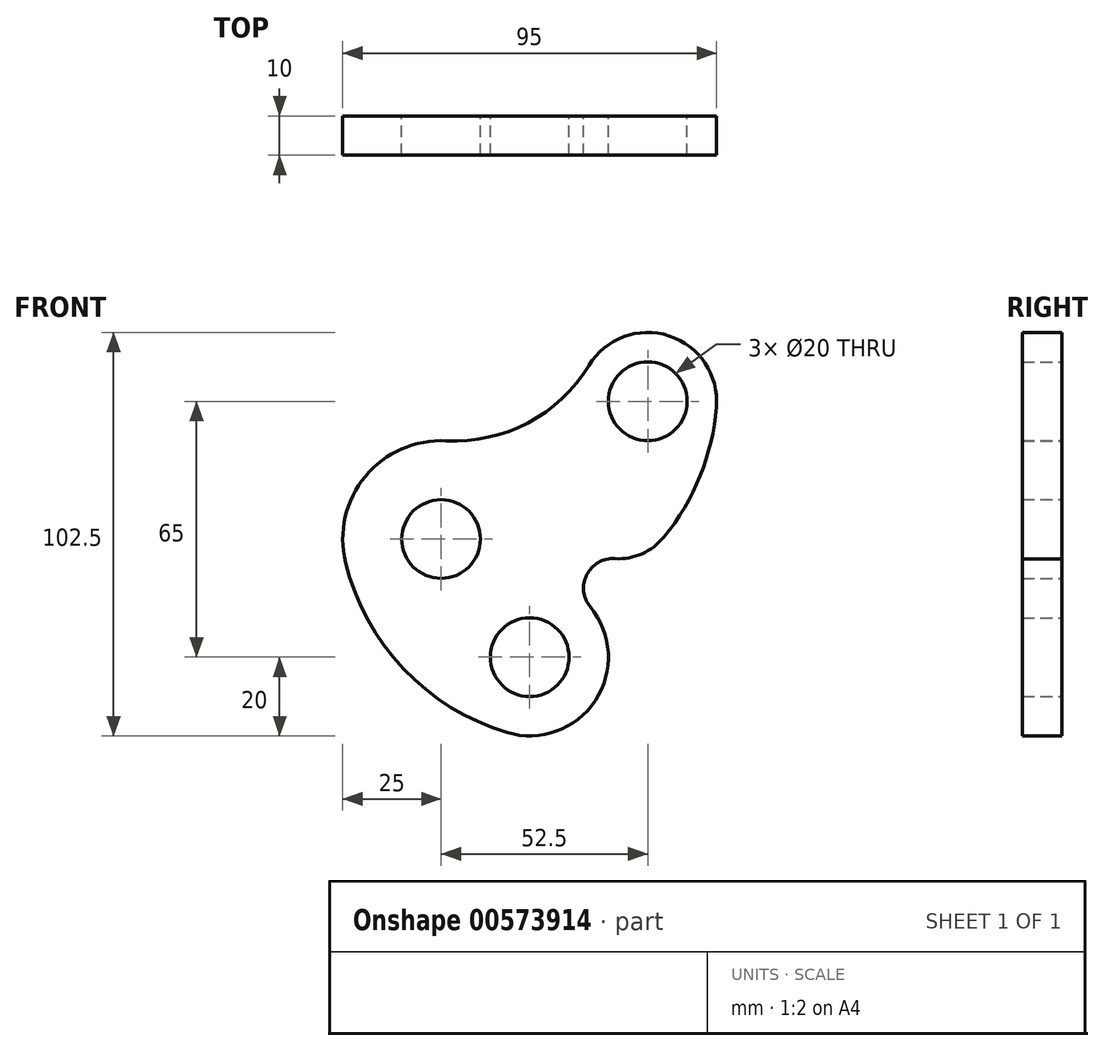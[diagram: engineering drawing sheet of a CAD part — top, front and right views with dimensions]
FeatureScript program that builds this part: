
annotation { "Feature Type Name" : "Feature", "Feature Type Description" : "" }
export const myFeature = defineFeature(function(context is Context, id is Id, definition is map)
    precondition{}
    {
        {
            var Q0;
            Q0=qCreatedBy(makeId("Front.planeOp"),FACE);
            var sketch = newSketch(context, id + "F0", { "sketchPlane" : qUnion([Q0])});
            skCircle(sketch, "E0", {"center": v(0, 0) * mm, "radius": 10 * mm});
            skCircle(sketch, "E1", {"center": v(22.5, -30) * mm, "radius": 10 * mm});
            skCircle(sketch, "E2", {"center": v(52.5, 35) * mm, "radius": 10 * mm});
            skArc(sketch, "E3", {"start": v(1.3, 24.97) * mm, "mid": v(-19.26, 15.94) * mm, "end": v(-24.28, -5.94) * mm});
            skArc(sketch, "E4", {"start": v(69.94, 33.58) * mm, "mid": v(57.9, 51.64) * mm, "end": v(37.55, 44.1) * mm});
            skArc(sketch, "E5", {"start": v(16.75, -49.16) * mm, "mid": v(39.17, -41.05) * mm, "end": v(37.9, -17.24) * mm});
            skArc(sketch, "E6", {"start": v(-24.28, -5.94) * mm, "mid": v(-9.51, -33) * mm, "end": v(16.75, -49.16) * mm});
            skArc(sketch, "E7", {"start": v(1.3, 24.97) * mm, "mid": v(22.07, 29.54) * mm, "end": v(37.55, 44.1) * mm});
            skArc(sketch, "E8", {"start": v(44.12, -4.97) * mm, "mid": v(37, -9.07) * mm, "end": v(37.9, -17.24) * mm});
            skArc(sketch, "E9", {"start": v(44.12, -4.97) * mm, "mid": v(51.03, -3.73) * mm, "end": v(56.62, 0.51) * mm});
            skArc(sketch, "E10", {"start": v(56.62, 0.51) * mm, "mid": v(65.8, 16.03) * mm, "end": v(69.94, 33.58) * mm});
            skSolve(sketch);
        }
        {
            var Q0;
            Q0 = qSketchRegion(id + "F0", true);
            extrude(context, id + "F1", {"entities" : qUnion([Q0]), "depth" : 10 * mm, "offsetDistance" : 25 * mm});
        }
    });
